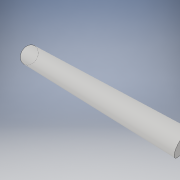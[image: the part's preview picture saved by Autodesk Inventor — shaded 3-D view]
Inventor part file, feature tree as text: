
AUTODESK INVENTOR PART (.ipt)
format: ipt  version: 2019 (Build 230136000, 136)  size: 90,112 bytes
history: native  units: in
note: dims shown in document units (in); Inventor stores cm internally (conversion verified against a paired STEP export)
features: extrude x1, sketch x1
ambient origin geometry x8: Origin, YZ Plane, XZ Plane, XY Plane, X Axis, Y Axis, Z Axis, Center Point
bodies: Solid1 (feature_tree)
feature tree (2):
  extrude  "Extrusion1"  Depth=4.0in TaperAngle=0.0deg
  sketch  "Sketch1"  dims[d0=0.5in d1=4.0in d2=0.0in]
